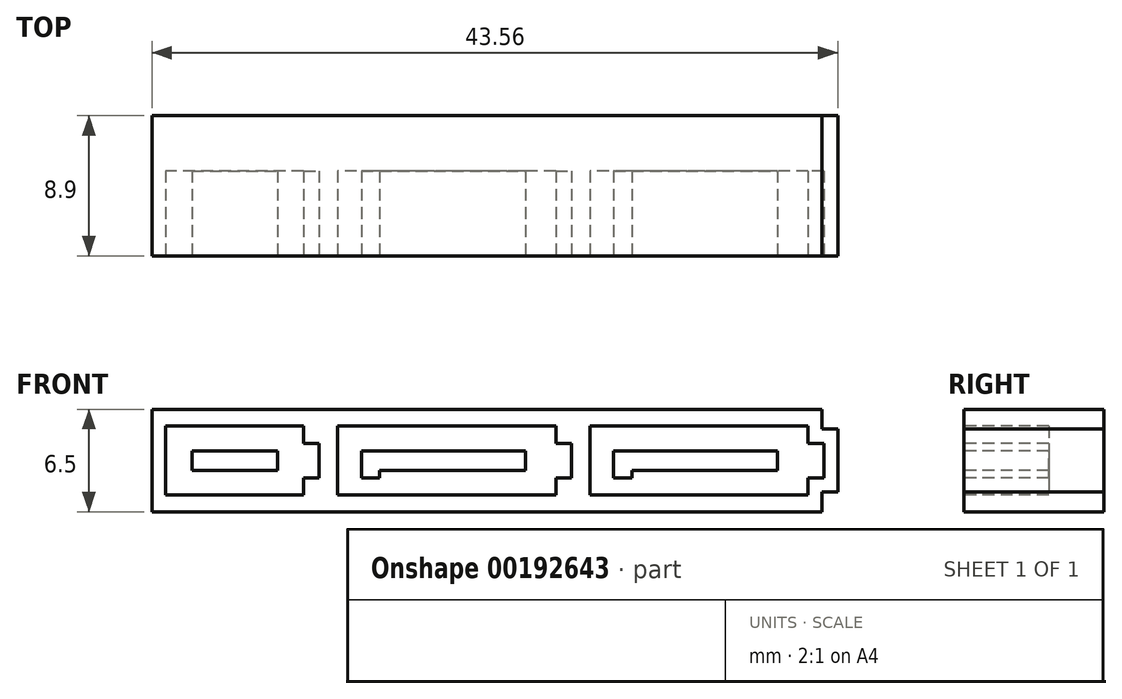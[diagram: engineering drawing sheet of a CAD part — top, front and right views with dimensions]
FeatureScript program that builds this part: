
annotation { "Feature Type Name" : "Feature", "Feature Type Description" : "" }
export const myFeature = defineFeature(function(context is Context, id is Id, definition is map)
    precondition{}
    {
        {
            var Q0;
            Q0=qCreatedBy(makeId("Front.planeOp"),FACE);
            var sketch = newSketch(context, id + "F0", { "sketchPlane" : qUnion([Q0])});
            skLineSegment(sketch, "E0.bottom", {"start": v(-21.78, 0) * mm, "end": v(20.78, 0) * mm});
            skLineSegment(sketch, "E0.top", {"start": v(-21.78, 6.5) * mm, "end": v(20.78, 6.5) * mm});
            skLineSegment(sketch, "E0.left", {"start": v(-21.78, 0) * mm, "end": v(-21.78, 6.5) * mm});
            skLineSegment(sketch, "E0.right", {"start": v(21.78, 1.25) * mm, "end": v(21.78, 5.25) * mm});
            skLineSegment(sketch, "E1.0", {"start": v(20.78, 0) * mm, "end": v(20.78, 1.25) * mm});
            skLineSegment(sketch, "E2.0", {"start": v(20.78, 5.25) * mm, "end": v(21.78, 5.25) * mm});
            skLineSegment(sketch, "E3.0", {"start": v(20.78, 1.25) * mm, "end": v(21.78, 1.25) * mm});
            skLineSegment(sketch, "E4.trimOffspring", {"start": v(20.78, 5.25) * mm, "end": v(20.78, 6.5) * mm});
            skSolve(sketch);
        }
        {
            var Q0;
            Q0 = qSketchRegion(id + "F0", true);
            extrude(context, id + "F1", {"entities" : qUnion([Q0]), "endBound" : BoundingType.SYMMETRIC, "depth" : 8.9 * mm});
        }
        {
            var Q0;
            Q0=makeQuery(id+"F1.opExtrude","CAP_FACE",FACE,{"disambiguationData":[OSD([sQuery(id+"F0.wireOp",EDGE,"E0.bottom"),sQuery(id+"F0.wireOp",EDGE,"E0.top"),sQuery(id+"F0.wireOp",EDGE,"E0.left"),sQuery(id+"F0.wireOp",EDGE,"E0.right"),sQuery(id+"F0.wireOp",EDGE,"E1.0"),sQuery(id+"F0.wireOp",EDGE,"E2.0"),sQuery(id+"F0.wireOp",EDGE,"E3.0"),sQuery(id+"F0.wireOp",EDGE,"E4.trimOffspring")])],"isStart":false});
            var sketch = newSketch(context, id + "F2", { "sketchPlane" : qUnion([Q0])});
            skLineSegment(sketch, "E5.0", {"start": v(19.9, 5.45) * mm, "end": v(6.05, 5.45) * mm});
            skLineSegment(sketch, "E5.1", {"start": v(19.9, 4.35) * mm, "end": v(19.9, 5.45) * mm});
            skLineSegment(sketch, "E5.2", {"start": v(-20.9, 5.45) * mm, "end": v(-20.9, 1.05) * mm});
            skLineSegment(sketch, "E5.3", {"start": v(20.9, 4.35) * mm, "end": v(19.9, 4.35) * mm});
            skLineSegment(sketch, "E5.4", {"start": v(-20.9, 1.05) * mm, "end": v(-12.15, 1.05) * mm});
            skLineSegment(sketch, "E5.5", {"start": v(19.9, 1.06) * mm, "end": v(19.9, 2.15) * mm});
            skLineSegment(sketch, "E5.6", {"start": v(19.9, 2.15) * mm, "end": v(20.9, 2.15) * mm});
            skLineSegment(sketch, "E5.7", {"start": v(20.9, 2.15) * mm, "end": v(20.9, 4.35) * mm});
            skLineSegment(sketch, "E6.0", {"start": v(-12.15, 5.45) * mm, "end": v(-12.15, 4.35) * mm});
            skLineSegment(sketch, "E7.0", {"start": v(-11.15, 4.35) * mm, "end": v(-11.15, 2.15) * mm});
            skLineSegment(sketch, "E8.0", {"start": v(-11.15, 4.35) * mm, "end": v(-12.15, 4.35) * mm});
            skLineSegment(sketch, "E9.0", {"start": v(-12.15, 2.15) * mm, "end": v(-11.15, 2.15) * mm});
            skLineSegment(sketch, "E10.trimOffspring", {"start": v(-12.15, 2.15) * mm, "end": v(-12.15, 1.05) * mm});
            skLineSegment(sketch, "E11", {"start": v(-9.97, 5.45) * mm, "end": v(-9.97, 1.06) * mm});
            skLineSegment(sketch, "E12.trimOffspring", {"start": v(-12.15, 5.45) * mm, "end": v(-20.9, 5.44) * mm});
            skLineSegment(sketch, "E13.trimOffspring", {"start": v(-9.97, 1.05) * mm, "end": v(3.87, 1.06) * mm});
            skLineSegment(sketch, "E14", {"start": v(3.87, 5.45) * mm, "end": v(3.87, 4.35) * mm});
            skLineSegment(sketch, "E15", {"start": v(3.87, 4.35) * mm, "end": v(4.88, 4.35) * mm});
            skLineSegment(sketch, "E16", {"start": v(4.88, 4.35) * mm, "end": v(4.88, 2.15) * mm});
            skLineSegment(sketch, "E17", {"start": v(4.87, 2.15) * mm, "end": v(3.87, 2.15) * mm});
            skLineSegment(sketch, "E18.trimOffspring", {"start": v(3.87, 2.15) * mm, "end": v(3.87, 1.06) * mm});
            skLineSegment(sketch, "E19", {"start": v(6.05, 5.45) * mm, "end": v(6.05, 1.06) * mm});
            skLineSegment(sketch, "E20.trimOffspring", {"start": v(6.05, 1.06) * mm, "end": v(19.9, 1.06) * mm});
            skLineSegment(sketch, "E21.trimOffspring", {"start": v(3.88, 5.45) * mm, "end": v(-9.97, 5.45) * mm});
            skLineSegment(sketch, "E22.bottom", {"start": v(-19.24, 3.86) * mm, "end": v(-13.81, 3.86) * mm});
            skLineSegment(sketch, "E22.top", {"start": v(-19.24, 2.63) * mm, "end": v(-13.81, 2.63) * mm});
            skLineSegment(sketch, "E22.left", {"start": v(-19.24, 3.86) * mm, "end": v(-19.24, 2.63) * mm});
            skLineSegment(sketch, "E22.right", {"start": v(-13.81, 3.86) * mm, "end": v(-13.81, 2.63) * mm});
            skLineSegment(sketch, "E23", {"start": v(-16.53, 2.63) * mm, "end": v(-16.53, 3.86) * mm, "construction": true});
            skLineSegment(sketch, "E24", {"start": v(-8.47, 3.87) * mm, "end": v(-8.47, 2.15) * mm});
            skLineSegment(sketch, "E25", {"start": v(-8.47, 2.15) * mm, "end": v(-7.32, 2.15) * mm});
            skLineSegment(sketch, "E26", {"start": v(-7.32, 2.15) * mm, "end": v(-7.32, 2.64) * mm});
            skLineSegment(sketch, "E27", {"start": v(-7.32, 2.64) * mm, "end": v(1.94, 2.64) * mm});
            skLineSegment(sketch, "E28", {"start": v(1.94, 2.64) * mm, "end": v(1.94, 3.87) * mm});
            skLineSegment(sketch, "E29", {"start": v(1.94, 3.87) * mm, "end": v(-8.47, 3.86) * mm});
            skLineSegment(sketch, "E30", {"start": v(-3.27, 3.87) * mm, "end": v(-3.27, 2.64) * mm, "construction": true});
            skLineSegment(sketch, "E31", {"start": v(7.55, 3.87) * mm, "end": v(7.55, 2.15) * mm});
            skLineSegment(sketch, "E32", {"start": v(7.55, 2.15) * mm, "end": v(8.7, 2.15) * mm});
            skLineSegment(sketch, "E33", {"start": v(8.7, 2.15) * mm, "end": v(8.7, 2.64) * mm});
            skLineSegment(sketch, "E34", {"start": v(8.7, 2.64) * mm, "end": v(17.96, 2.64) * mm});
            skLineSegment(sketch, "E35", {"start": v(17.96, 2.64) * mm, "end": v(17.96, 3.87) * mm});
            skLineSegment(sketch, "E36", {"start": v(17.96, 3.87) * mm, "end": v(7.55, 3.87) * mm});
            skLineSegment(sketch, "E37", {"start": v(12.76, 3.87) * mm, "end": v(12.76, 2.64) * mm, "construction": true});
            skLineSegment(sketch, "E38", {"start": v(-21.78, 3.25) * mm, "end": v(21.78, 3.25) * mm, "construction": true});
            skLineSegment(sketch, "E39", {"start": v(-11.15, 4.35) * mm, "end": v(-9.97, 4.35) * mm, "construction": true});
            skLineSegment(sketch, "E40", {"start": v(4.88, 4.35) * mm, "end": v(6.05, 4.35) * mm, "construction": true});
            skSolve(sketch);
        }
        {
            var Q0;
            Q0 = qSketchRegion(id + "F2", true);
            extrude(context, id + "F3", {"entities" : qUnion([Q0]), "operationType" : NewBodyOperationType.REMOVE, "oppositeDirection" : true, "depth" : 5.4 * mm});
        }
    });
